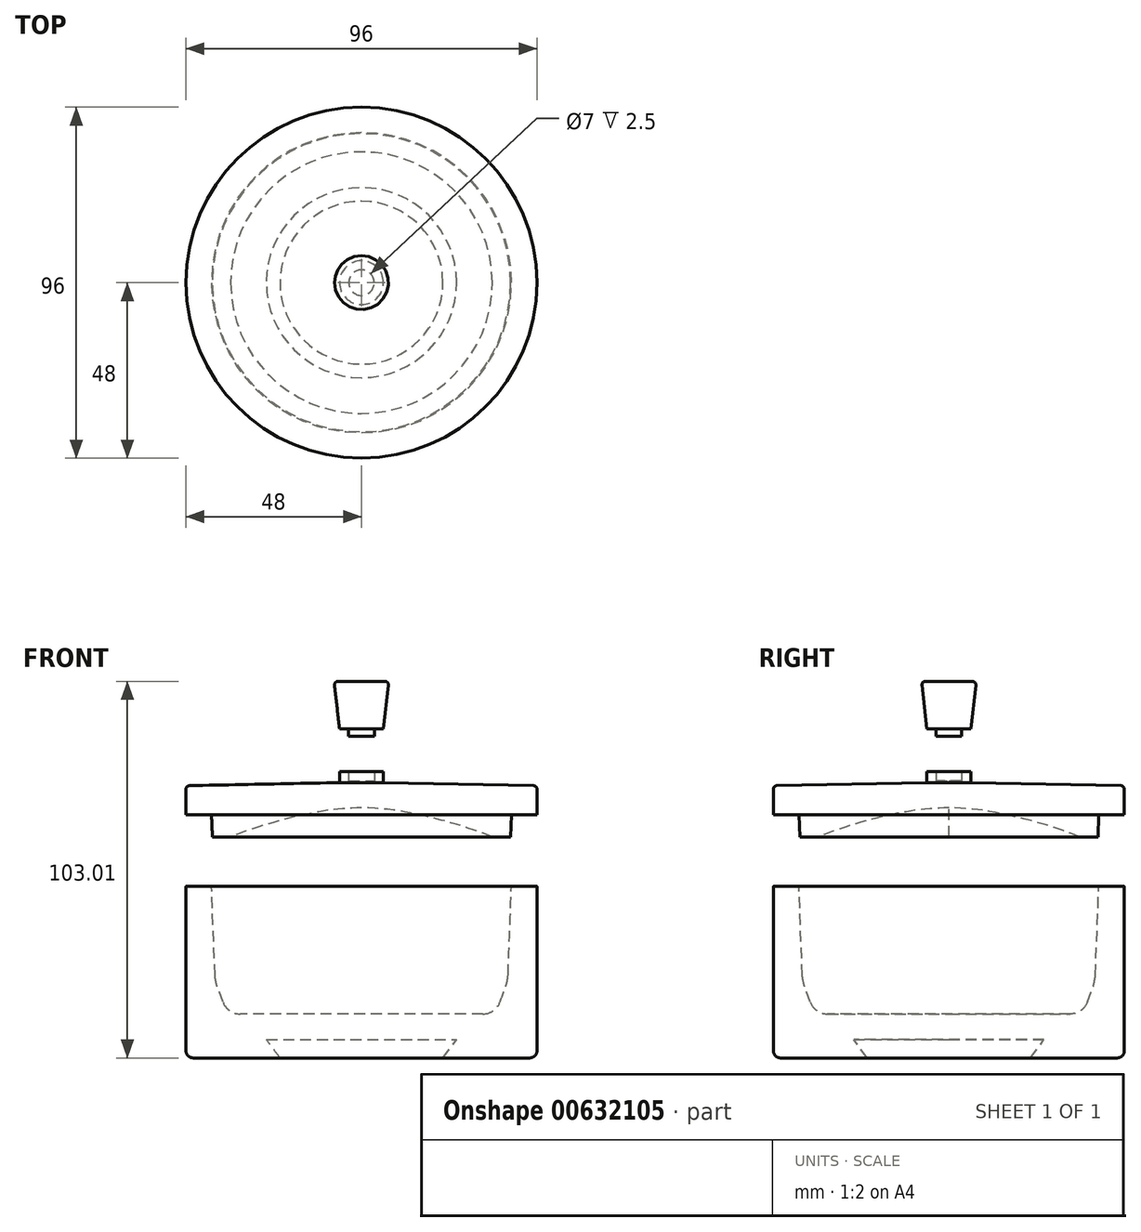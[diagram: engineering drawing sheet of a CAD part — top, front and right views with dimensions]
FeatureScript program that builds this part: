
annotation { "Feature Type Name" : "Feature", "Feature Type Description" : "" }
export const myFeature = defineFeature(function(context is Context, id is Id, definition is map)
    precondition{}
    {
        {
            var Q0;
            Q0=qCreatedBy(makeId("Front.planeOp"),FACE);
            var sketch = newSketch(context, id + "F0", { "sketchPlane" : qUnion([Q0])});
            skLineSegment(sketch, "E0", {"start": v(0, -15.08) * mm, "end": v(0, -1.98) * mm, "construction": true});
            skLineSegment(sketch, "E1", {"start": v(0, -67.3) * mm, "end": v(26, -67.3) * mm});
            skLineSegment(sketch, "E2", {"start": v(26, -67.3) * mm, "end": v(22.26, -72.3) * mm});
            skLineSegment(sketch, "E3", {"start": v(22.26, -72.3) * mm, "end": v(48, -72.3) * mm});
            skLineSegment(sketch, "E4", {"start": v(48, -72.3) * mm, "end": v(48, -25.3) * mm});
            skLineSegment(sketch, "E5", {"start": v(48, -25.3) * mm, "end": v(41, -25.3) * mm});
            skLineSegment(sketch, "E6", {"start": v(41, -25.3) * mm, "end": v(39.66, -60.27) * mm});
            skLineSegment(sketch, "E7", {"start": v(39.66, -60.27) * mm, "end": v(0, -60.27) * mm});
            skLineSegment(sketch, "E8", {"start": v(0, -60.27) * mm, "end": v(0, -67.3) * mm});
            skLineSegment(sketch, "E9", {"start": v(48, -5.86) * mm, "end": v(41, -5.86) * mm});
            skLineSegment(sketch, "E10", {"start": v(41, -5.86) * mm, "end": v(40.77, -11.86) * mm});
            skLineSegment(sketch, "E11", {"start": v(48, -5.86) * mm, "end": v(48, 2.14) * mm});
            skLineSegment(sketch, "E12", {"start": v(48, 2.14) * mm, "end": v(6, 2.99) * mm});
            skLineSegment(sketch, "E13", {"start": v(40.77, -11.86) * mm, "end": v(35.77, -11.86) * mm});
            skFitSpline(sketch, "E14", {"points": [v(35.77, -11.86) * mm, v(18.37, -6.41) * mm, v(0, -3.9) * mm], "startDerivative": vector(-41.03, 16.4) * mm, "endDerivative": vector(-44.72, 0.58) * mm});
            skLineSegment(sketch, "E15", {"start": v(0, -1.98) * mm, "end": v(0, -3.9) * mm});
            skLineSegment(sketch, "E16", {"start": v(0, 33.24) * mm, "end": v(0, 17.3) * mm});
            skLineSegment(sketch, "E17", {"start": v(0, 15.7) * mm, "end": v(3.5, 15.7) * mm});
            skLineSegment(sketch, "E18", {"start": v(3.5, 15.7) * mm, "end": v(3.5, 17.7) * mm});
            skLineSegment(sketch, "E19", {"start": v(0, 17.3) * mm, "end": v(0, 15.7) * mm});
            skLineSegment(sketch, "E20.trimOffspring", {"start": v(0, 3.11) * mm, "end": v(0, 81.56) * mm, "construction": true});
            skLineSegment(sketch, "E21", {"start": v(6, 2.99) * mm, "end": v(6, 5.99) * mm});
            skLineSegment(sketch, "E22", {"start": v(0, 5.61) * mm, "end": v(0, -3.9) * mm});
            skLineSegment(sketch, "E23", {"start": v(0, 3.49) * mm, "end": v(3.5, 3.49) * mm});
            skLineSegment(sketch, "E24", {"start": v(3.5, 3.49) * mm, "end": v(3.5, 5.99) * mm});
            skLineSegment(sketch, "E25", {"start": v(3.5, 5.99) * mm, "end": v(6, 5.99) * mm});
            skLineSegment(sketch, "E26", {"start": v(3.5, 17.7) * mm, "end": v(6, 17.7) * mm});
            skLineSegment(sketch, "E27", {"start": v(6, 17.7) * mm, "end": v(7.37, 29.6) * mm});
            skLineSegment(sketch, "E28", {"start": v(6.38, 30.7) * mm, "end": v(0, 30.7) * mm});
            skPoint(sketch, "E29.visualSharp", {"position": v(7.5, 30.7) * mm});
            skArc(sketch, "E29.filletArc", {"start": v(7.37, 29.6) * mm, "mid": v(7.12, 30.37) * mm, "end": v(6.38, 30.7) * mm});
            skSolve(sketch);
        }
        {
            var Q0;
            Q0 = qSketchRegion(id + "F0", true);
            var Q1;
            Q1=sQuery(id+"F0.wireOp",EDGE,"E0");
            revolve(context, id + "F1", {"entities" : qUnion([Q0]), "axis" : qUnion([Q1]), "revolveType" : RevolveType.FULL});
        }
        {
            var Q0;
            Q0=makeQuery(id+"F1.opRevolve","SWEPT_EDGE",EDGE,{"disambiguationData":[OSD([sQuery(id+"F0.wireOp",EDGE,"E5"),sQuery(id+"F0.wireOp",EDGE,"E6")])]});
            var Q1;
            Q1=makeQuery(id+"F1.opRevolve","SWEPT_EDGE",EDGE,{"disambiguationData":[OSD([sQuery(id+"F0.wireOp",EDGE,"E4"),sQuery(id+"F0.wireOp",EDGE,"E5")])]});
            fillet(context, id + "F2", {"entities" : qUnion([Q0, Q1]), "radius" : 0.2 * mm, "tangentPropagation" : true, "allowEdgeOverflow" : false});
        }
        {
            var Q0;
            Q0=makeQuery(id+"F1.opRevolve","SWEPT_EDGE",EDGE,{"disambiguationData":[OSD([sQuery(id+"F0.wireOp",EDGE,"E3"),sQuery(id+"F0.wireOp",EDGE,"E4")])]});
            fillet(context, id + "F3", {"entities" : qUnion([Q0]), "radius" : 2 * mm, "tangentPropagation" : true, "allowEdgeOverflow" : false});
        }
        {
            var Q0;
            Q0=makeQuery(id+"F1.opRevolve","SWEPT_EDGE",EDGE,{"disambiguationData":[OSD([sQuery(id+"F0.wireOp",EDGE,"E6"),sQuery(id+"F0.wireOp",EDGE,"E7")])]});
            chamfer(context, id + "F4", {"entities" : qUnion([Q0]), "chamferType" : ChamferType.TWO_OFFSETS, "width1" : 9 * mm, "oppositeDirection" : false, "width2" : 3 * mm, "tangentPropagation" : true});
        }
        {
            var Q0;
            {var subQ0=sQuery(id+"F0.wireOp",EDGE,"E7");Q0=makeQuery(id+"F4.opChamfer","BLEND_EDGE",EDGE,{"blendedFrom":[makeQuery(id+"F1.opRevolve","SWEPT_EDGE",EDGE,{"disambiguationData":[OSD([sQuery(id+"F0.wireOp",EDGE,"E6"),subQ0])]}),makeQuery(id+"F1.opRevolve","SWEPT_FACE",FACE,{"disambiguationData":[OSD([subQ0])]})],"blendedInto":[makeQuery(id+"F1.opRevolve","SWEPT_FACE",FACE,{"disambiguationData":[OSD([subQ0])]})]});}
            fillet(context, id + "F5", {"entities" : qUnion([Q0]), "radius" : 5 * mm, "tangentPropagation" : true, "allowEdgeOverflow" : false});
        }
        {
            var Q0;
            {var subQ0=sQuery(id+"F0.wireOp",EDGE,"E6");Q0=makeQuery(id+"F4.opChamfer","BLEND_EDGE",EDGE,{"blendedFrom":[makeQuery(id+"F1.opRevolve","SWEPT_EDGE",EDGE,{"disambiguationData":[OSD([subQ0,sQuery(id+"F0.wireOp",EDGE,"E7")])]}),makeQuery(id+"F1.opRevolve","SWEPT_FACE",FACE,{"disambiguationData":[OSD([subQ0])]})],"blendedInto":[makeQuery(id+"F1.opRevolve","SWEPT_FACE",FACE,{"disambiguationData":[OSD([subQ0])]})]});}
            fillet(context, id + "F6", {"entities" : qUnion([Q0]), "radius" : 10 * mm, "tangentPropagation" : true, "rho" : 0.3, "crossSection" : FilletCrossSection.CONIC, "allowEdgeOverflow" : false});
        }
        {
            var Q0;
            Q0=makeQuery(id+"F1.opRevolve","SWEPT_EDGE",EDGE,{"disambiguationData":[OSD([sQuery(id+"F0.wireOp",EDGE,"E11"),sQuery(id+"F0.wireOp",EDGE,"E12")])]});
            fillet(context, id + "F7", {"entities" : qUnion([Q0]), "radius" : 1 * mm, "tangentPropagation" : true, "allowEdgeOverflow" : false});
        }
    });
